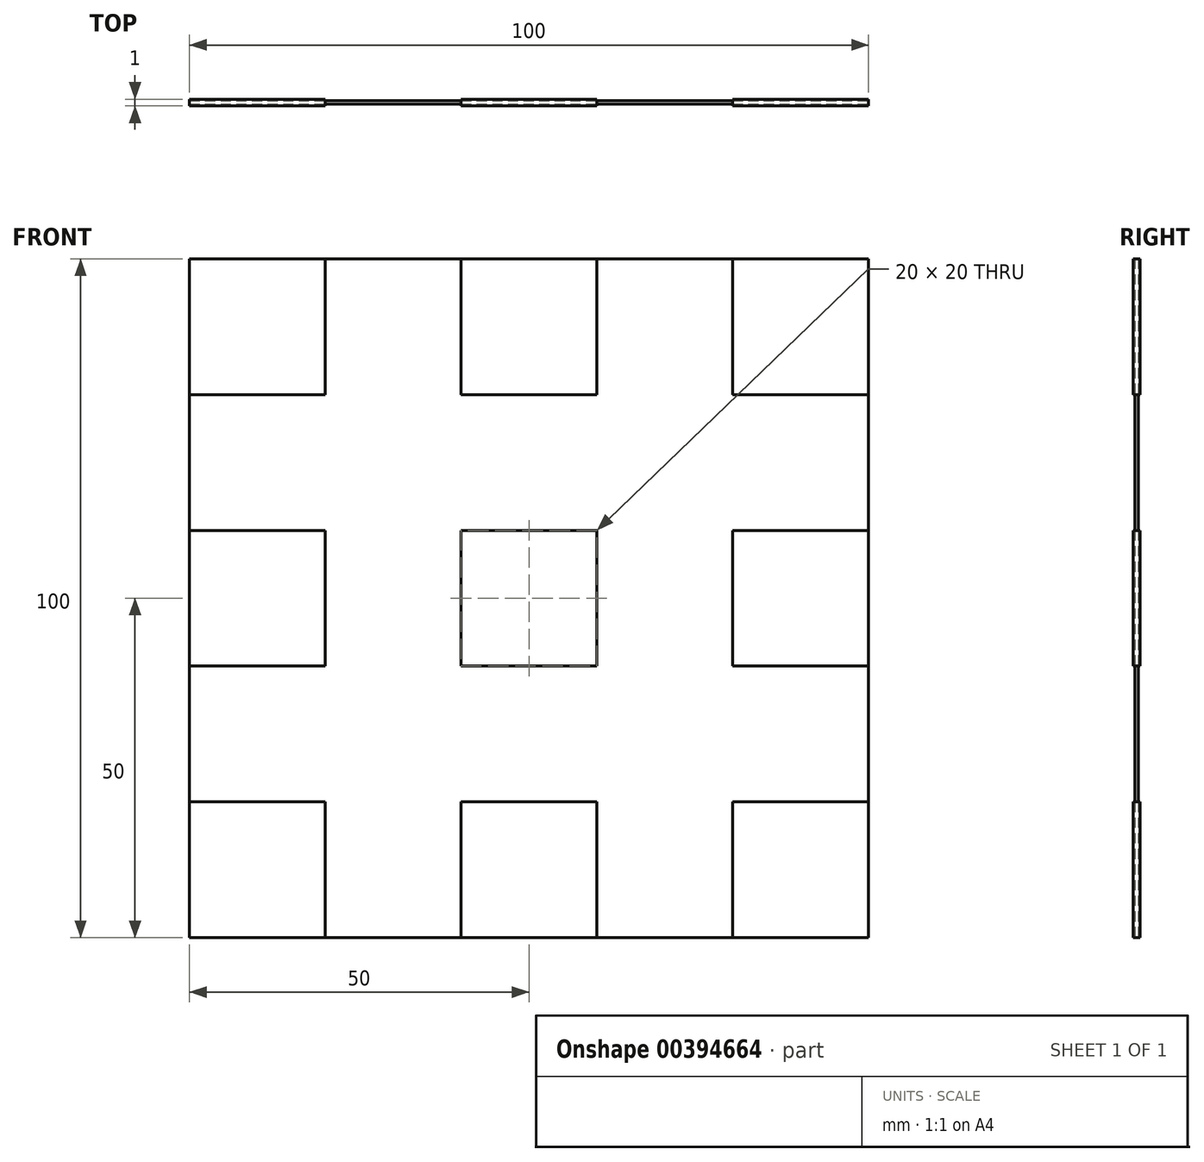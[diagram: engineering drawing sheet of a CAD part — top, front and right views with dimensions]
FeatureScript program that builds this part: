
annotation { "Feature Type Name" : "Feature", "Feature Type Description" : "" }
export const myFeature = defineFeature(function(context is Context, id is Id, definition is map)
    precondition{}
    {
        {
            var Q0;
            Q0=qCreatedBy(makeId("Front.planeOp"),FACE);
            var sketch = newSketch(context, id + "F0", { "sketchPlane" : qUnion([Q0])});
            skLineSegment(sketch, "E0.bottom", {"start": v(50, -50) * mm, "end": v(-50, -50) * mm});
            skLineSegment(sketch, "E0.top", {"start": v(50, 50) * mm, "end": v(-50, 50) * mm});
            skLineSegment(sketch, "E0.left", {"start": v(50, -50) * mm, "end": v(50, 50) * mm});
            skLineSegment(sketch, "E0.right", {"start": v(-50, -50) * mm, "end": v(-50, 50) * mm});
            skPoint(sketch, "E0.middle", {"position": v(0, 0) * mm});
            skLineSegment(sketch, "E1", {"start": v(-30, 50) * mm, "end": v(-30, -50) * mm});
            skLineSegment(sketch, "E2", {"start": v(-10, 50) * mm, "end": v(-10, -50) * mm});
            skLineSegment(sketch, "E3", {"start": v(10, 50) * mm, "end": v(10, -50) * mm});
            skLineSegment(sketch, "E4", {"start": v(30, 50) * mm, "end": v(30, -50) * mm});
            skLineSegment(sketch, "E5", {"start": v(-50, 30) * mm, "end": v(50, 30) * mm});
            skLineSegment(sketch, "E6", {"start": v(-50, 10) * mm, "end": v(50, 10) * mm});
            skLineSegment(sketch, "E7", {"start": v(-50, -10) * mm, "end": v(50, -10) * mm});
            skLineSegment(sketch, "E8", {"start": v(-50, -30) * mm, "end": v(50, -30) * mm});
            skSolve(sketch);
        }
        {
            var Q0;
            {var subQ0=sQuery(id+"F0.wireOp",EDGE,"E0.right");var subQ1=sQuery(id+"F0.wireOp",EDGE,"E0.top");var subQ2=makeQuery(id+"F0.imprint","INTERSECT",VERTEX,{"derivedFrom":[subQ1,subQ0]});Q0=makeQuery(id+"F0.imprint","IMPRINT",FACE,{"disambiguationData":[TD([[makeQuery(id+"F0.imprint","IMPRINT",EDGE,{"disambiguationData":[TD([[subQ2,1.0]])],"derivedFrom":subQ1}),1.0]])]});}
            var Q1;
            {var subQ0=sQuery(id+"F0.wireOp",EDGE,"E2");var subQ1=sQuery(id+"F0.wireOp",EDGE,"E0.top");var subQ2=makeQuery(id+"F0.imprint","INTERSECT",VERTEX,{"derivedFrom":[subQ1,subQ0]});Q1=makeQuery(id+"F0.imprint","IMPRINT",FACE,{"disambiguationData":[TD([[makeQuery(id+"F0.imprint","IMPRINT",EDGE,{"disambiguationData":[TD([[subQ2,1.0]])],"derivedFrom":subQ1}),1.0]])]});}
            var Q2;
            {var subQ0=sQuery(id+"F0.wireOp",EDGE,"E0.left");var subQ1=sQuery(id+"F0.wireOp",EDGE,"E0.top");var subQ2=makeQuery(id+"F0.imprint","INTERSECT",VERTEX,{"derivedFrom":[subQ1,subQ0]});Q2=makeQuery(id+"F0.imprint","IMPRINT",FACE,{"disambiguationData":[TD([[makeQuery(id+"F0.imprint","IMPRINT",EDGE,{"disambiguationData":[TD([[subQ2,-1.0]])],"derivedFrom":subQ1}),1.0]])]});}
            var Q3;
            {var subQ0=sQuery(id+"F0.wireOp",EDGE,"E6");var subQ1=sQuery(id+"F0.wireOp",EDGE,"E0.right");var subQ2=makeQuery(id+"F0.imprint","INTERSECT",VERTEX,{"derivedFrom":[subQ1,subQ0]});Q3=makeQuery(id+"F0.imprint","IMPRINT",FACE,{"disambiguationData":[TD([[makeQuery(id+"F0.imprint","IMPRINT",EDGE,{"disambiguationData":[TD([[subQ2,1.0]])],"derivedFrom":subQ1}),-1.0]])]});}
            var Q4;
            {var subQ0=sQuery(id+"F0.wireOp",EDGE,"E6");var subQ1=sQuery(id+"F0.wireOp",EDGE,"E2");var subQ2=makeQuery(id+"F0.imprint","INTERSECT",VERTEX,{"derivedFrom":[subQ1,subQ0]});Q4=makeQuery(id+"F0.imprint","IMPRINT",FACE,{"disambiguationData":[TD([[makeQuery(id+"F0.imprint","IMPRINT",EDGE,{"disambiguationData":[TD([[subQ2,-1.0]])],"derivedFrom":subQ1}),1.0]])]});}
            var Q5;
            {var subQ0=sQuery(id+"F0.wireOp",EDGE,"E6");var subQ1=sQuery(id+"F0.wireOp",EDGE,"E0.left");var subQ2=makeQuery(id+"F0.imprint","INTERSECT",VERTEX,{"derivedFrom":[subQ1,subQ0]});Q5=makeQuery(id+"F0.imprint","IMPRINT",FACE,{"disambiguationData":[TD([[makeQuery(id+"F0.imprint","IMPRINT",EDGE,{"disambiguationData":[TD([[subQ2,1.0]])],"derivedFrom":subQ1}),1.0]])]});}
            var Q6;
            {var subQ0=sQuery(id+"F0.wireOp",EDGE,"E0.right");var subQ1=sQuery(id+"F0.wireOp",EDGE,"E0.bottom");var subQ2=makeQuery(id+"F0.imprint","INTERSECT",VERTEX,{"derivedFrom":[subQ1,subQ0]});Q6=makeQuery(id+"F0.imprint","IMPRINT",FACE,{"disambiguationData":[TD([[makeQuery(id+"F0.imprint","IMPRINT",EDGE,{"disambiguationData":[TD([[subQ2,1.0]])],"derivedFrom":subQ1}),-1.0]])]});}
            var Q7;
            {var subQ0=sQuery(id+"F0.wireOp",EDGE,"E2");var subQ1=sQuery(id+"F0.wireOp",EDGE,"E0.bottom");var subQ2=makeQuery(id+"F0.imprint","INTERSECT",VERTEX,{"derivedFrom":[subQ1,subQ0]});Q7=makeQuery(id+"F0.imprint","IMPRINT",FACE,{"disambiguationData":[TD([[makeQuery(id+"F0.imprint","IMPRINT",EDGE,{"disambiguationData":[TD([[subQ2,1.0]])],"derivedFrom":subQ1}),-1.0]])]});}
            var Q8;
            {var subQ0=sQuery(id+"F0.wireOp",EDGE,"E0.left");var subQ1=sQuery(id+"F0.wireOp",EDGE,"E0.bottom");var subQ2=makeQuery(id+"F0.imprint","INTERSECT",VERTEX,{"derivedFrom":[subQ1,subQ0]});Q8=makeQuery(id+"F0.imprint","IMPRINT",FACE,{"disambiguationData":[TD([[makeQuery(id+"F0.imprint","IMPRINT",EDGE,{"disambiguationData":[TD([[subQ2,-1.0]])],"derivedFrom":subQ1}),-1.0]])]});}
            extrude(context, id + "F1", {"entities" : qUnion([Q0, Q1, Q2, Q3, Q4, Q5, Q6, Q7, Q8]), "endBound" : BoundingType.SYMMETRIC, "depth" : 1 * mm});
        }
        {
            var Q0;
            {var subQ0=sQuery(id+"F0.wireOp",EDGE,"E1");var subQ1=sQuery(id+"F0.wireOp",EDGE,"E0.top");var subQ2=makeQuery(id+"F0.imprint","INTERSECT",VERTEX,{"derivedFrom":[subQ1,subQ0]});Q0=makeQuery(id+"F0.imprint","IMPRINT",FACE,{"disambiguationData":[TD([[makeQuery(id+"F0.imprint","IMPRINT",EDGE,{"disambiguationData":[TD([[subQ2,1.0]])],"derivedFrom":subQ1}),1.0]])]});}
            var Q1;
            {var subQ0=sQuery(id+"F0.wireOp",EDGE,"E5");var subQ1=sQuery(id+"F0.wireOp",EDGE,"E0.right");var subQ2=makeQuery(id+"F0.imprint","INTERSECT",VERTEX,{"derivedFrom":[subQ1,subQ0]});Q1=makeQuery(id+"F0.imprint","IMPRINT",FACE,{"disambiguationData":[TD([[makeQuery(id+"F0.imprint","IMPRINT",EDGE,{"disambiguationData":[TD([[subQ2,1.0]])],"derivedFrom":subQ1}),-1.0]])]});}
            var Q2;
            {var subQ0=sQuery(id+"F0.wireOp",EDGE,"E5");var subQ1=sQuery(id+"F0.wireOp",EDGE,"E1");var subQ2=makeQuery(id+"F0.imprint","INTERSECT",VERTEX,{"derivedFrom":[subQ1,subQ0]});Q2=makeQuery(id+"F0.imprint","IMPRINT",FACE,{"disambiguationData":[TD([[makeQuery(id+"F0.imprint","IMPRINT",EDGE,{"disambiguationData":[TD([[subQ2,-1.0]])],"derivedFrom":subQ1}),1.0]])]});}
            var Q3;
            {var subQ0=sQuery(id+"F0.wireOp",EDGE,"E3");var subQ1=sQuery(id+"F0.wireOp",EDGE,"E0.top");var subQ2=makeQuery(id+"F0.imprint","INTERSECT",VERTEX,{"derivedFrom":[subQ1,subQ0]});Q3=makeQuery(id+"F0.imprint","IMPRINT",FACE,{"disambiguationData":[TD([[makeQuery(id+"F0.imprint","IMPRINT",EDGE,{"disambiguationData":[TD([[subQ2,1.0]])],"derivedFrom":subQ1}),1.0]])]});}
            var Q4;
            {var subQ0=sQuery(id+"F0.wireOp",EDGE,"E5");var subQ1=sQuery(id+"F0.wireOp",EDGE,"E3");var subQ2=makeQuery(id+"F0.imprint","INTERSECT",VERTEX,{"derivedFrom":[subQ1,subQ0]});Q4=makeQuery(id+"F0.imprint","IMPRINT",FACE,{"disambiguationData":[TD([[makeQuery(id+"F0.imprint","IMPRINT",EDGE,{"disambiguationData":[TD([[subQ2,-1.0]])],"derivedFrom":subQ1}),1.0]])]});}
            var Q5;
            {var subQ0=sQuery(id+"F0.wireOp",EDGE,"E5");var subQ1=sQuery(id+"F0.wireOp",EDGE,"E2");var subQ2=makeQuery(id+"F0.imprint","INTERSECT",VERTEX,{"derivedFrom":[subQ1,subQ0]});Q5=makeQuery(id+"F0.imprint","IMPRINT",FACE,{"disambiguationData":[TD([[makeQuery(id+"F0.imprint","IMPRINT",EDGE,{"disambiguationData":[TD([[subQ2,-1.0]])],"derivedFrom":subQ1}),1.0]])]});}
            var Q6;
            {var subQ0=sQuery(id+"F0.wireOp",EDGE,"E5");var subQ1=sQuery(id+"F0.wireOp",EDGE,"E0.left");var subQ2=makeQuery(id+"F0.imprint","INTERSECT",VERTEX,{"derivedFrom":[subQ1,subQ0]});Q6=makeQuery(id+"F0.imprint","IMPRINT",FACE,{"disambiguationData":[TD([[makeQuery(id+"F0.imprint","IMPRINT",EDGE,{"disambiguationData":[TD([[subQ2,1.0]])],"derivedFrom":subQ1}),1.0]])]});}
            var Q7;
            {var subQ0=sQuery(id+"F0.wireOp",EDGE,"E6");var subQ1=sQuery(id+"F0.wireOp",EDGE,"E3");var subQ2=makeQuery(id+"F0.imprint","INTERSECT",VERTEX,{"derivedFrom":[subQ1,subQ0]});Q7=makeQuery(id+"F0.imprint","IMPRINT",FACE,{"disambiguationData":[TD([[makeQuery(id+"F0.imprint","IMPRINT",EDGE,{"disambiguationData":[TD([[subQ2,-1.0]])],"derivedFrom":subQ1}),1.0]])]});}
            var Q8;
            {var subQ0=sQuery(id+"F0.wireOp",EDGE,"E6");var subQ1=sQuery(id+"F0.wireOp",EDGE,"E1");var subQ2=makeQuery(id+"F0.imprint","INTERSECT",VERTEX,{"derivedFrom":[subQ1,subQ0]});Q8=makeQuery(id+"F0.imprint","IMPRINT",FACE,{"disambiguationData":[TD([[makeQuery(id+"F0.imprint","IMPRINT",EDGE,{"disambiguationData":[TD([[subQ2,-1.0]])],"derivedFrom":subQ1}),1.0]])]});}
            var Q9;
            {var subQ0=sQuery(id+"F0.wireOp",EDGE,"E7");var subQ1=sQuery(id+"F0.wireOp",EDGE,"E0.right");var subQ2=makeQuery(id+"F0.imprint","INTERSECT",VERTEX,{"derivedFrom":[subQ1,subQ0]});Q9=makeQuery(id+"F0.imprint","IMPRINT",FACE,{"disambiguationData":[TD([[makeQuery(id+"F0.imprint","IMPRINT",EDGE,{"disambiguationData":[TD([[subQ2,1.0]])],"derivedFrom":subQ1}),-1.0]])]});}
            var Q10;
            {var subQ0=sQuery(id+"F0.wireOp",EDGE,"E7");var subQ1=sQuery(id+"F0.wireOp",EDGE,"E1");var subQ2=makeQuery(id+"F0.imprint","INTERSECT",VERTEX,{"derivedFrom":[subQ1,subQ0]});Q10=makeQuery(id+"F0.imprint","IMPRINT",FACE,{"disambiguationData":[TD([[makeQuery(id+"F0.imprint","IMPRINT",EDGE,{"disambiguationData":[TD([[subQ2,-1.0]])],"derivedFrom":subQ1}),1.0]])]});}
            var Q11;
            {var subQ0=sQuery(id+"F0.wireOp",EDGE,"E7");var subQ1=sQuery(id+"F0.wireOp",EDGE,"E2");var subQ2=makeQuery(id+"F0.imprint","INTERSECT",VERTEX,{"derivedFrom":[subQ1,subQ0]});Q11=makeQuery(id+"F0.imprint","IMPRINT",FACE,{"disambiguationData":[TD([[makeQuery(id+"F0.imprint","IMPRINT",EDGE,{"disambiguationData":[TD([[subQ2,-1.0]])],"derivedFrom":subQ1}),1.0]])]});}
            var Q12;
            {var subQ0=sQuery(id+"F0.wireOp",EDGE,"E7");var subQ1=sQuery(id+"F0.wireOp",EDGE,"E3");var subQ2=makeQuery(id+"F0.imprint","INTERSECT",VERTEX,{"derivedFrom":[subQ1,subQ0]});Q12=makeQuery(id+"F0.imprint","IMPRINT",FACE,{"disambiguationData":[TD([[makeQuery(id+"F0.imprint","IMPRINT",EDGE,{"disambiguationData":[TD([[subQ2,-1.0]])],"derivedFrom":subQ1}),1.0]])]});}
            var Q13;
            {var subQ0=sQuery(id+"F0.wireOp",EDGE,"E7");var subQ1=sQuery(id+"F0.wireOp",EDGE,"E0.left");var subQ2=makeQuery(id+"F0.imprint","INTERSECT",VERTEX,{"derivedFrom":[subQ1,subQ0]});Q13=makeQuery(id+"F0.imprint","IMPRINT",FACE,{"disambiguationData":[TD([[makeQuery(id+"F0.imprint","IMPRINT",EDGE,{"disambiguationData":[TD([[subQ2,1.0]])],"derivedFrom":subQ1}),1.0]])]});}
            var Q14;
            {var subQ0=sQuery(id+"F0.wireOp",EDGE,"E3");var subQ1=sQuery(id+"F0.wireOp",EDGE,"E0.bottom");var subQ2=makeQuery(id+"F0.imprint","INTERSECT",VERTEX,{"derivedFrom":[subQ1,subQ0]});Q14=makeQuery(id+"F0.imprint","IMPRINT",FACE,{"disambiguationData":[TD([[makeQuery(id+"F0.imprint","IMPRINT",EDGE,{"disambiguationData":[TD([[subQ2,1.0]])],"derivedFrom":subQ1}),-1.0]])]});}
            var Q15;
            {var subQ0=sQuery(id+"F0.wireOp",EDGE,"E1");var subQ1=sQuery(id+"F0.wireOp",EDGE,"E0.bottom");var subQ2=makeQuery(id+"F0.imprint","INTERSECT",VERTEX,{"derivedFrom":[subQ1,subQ0]});Q15=makeQuery(id+"F0.imprint","IMPRINT",FACE,{"disambiguationData":[TD([[makeQuery(id+"F0.imprint","IMPRINT",EDGE,{"disambiguationData":[TD([[subQ2,1.0]])],"derivedFrom":subQ1}),-1.0]])]});}
            extrude(context, id + "F2", {"entities" : qUnion([Q0, Q1, Q2, Q3, Q4, Q5, Q6, Q7, Q8, Q9, Q10, Q11, Q12, Q13, Q14, Q15]), "endBound" : BoundingType.SYMMETRIC, "depth" : 0.5 * mm});
        }
    });
